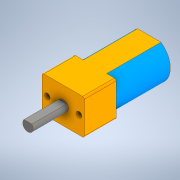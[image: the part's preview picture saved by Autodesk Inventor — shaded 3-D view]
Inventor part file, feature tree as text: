
AUTODESK INVENTOR PART (.ipt)
format: ipt  version: 2020 (Build 240168000, 168)  size: 167,424 bytes
history: native  units: mm
features: extrude x6, sketch x4, projected_geometry x2, fillet x1
ambient origin geometry x8: Origin, YZ Plane, XZ Plane, XY Plane, X Axis, Y Axis, Z Axis, Center Point
bodies: Solid1 (feature_tree)
feature tree (13):
  sketch  "Sketch1"  dims[d0=10.0mm d1=12.0mm]
  extrude  "Extrusion1"  Depth=12.0mm
  extrude  "Extrusion2"  Depth=9.0mm
  extrude  "Extrusion3"  Depth=9.0mm TaperAngle=0.0deg
  extrude  "Extrusion4"  Depth=10.0mm TaperAngle=0.0deg
  extrude  "Extrusion5"  Depth=0.5mm
  extrude  "Extrusion6"  Depth=9.8mm TaperAngle=0.0deg
  fillet  "Fillet1"  Radius=15.4mm
  sketch  "Sketch2"  dims[d2=9.0mm d3=1.6mm]
  projected_geometry  "Projected Loop1"
  sketch  "Sketch3"  dims[d4=3.0mm d5=9.0mm d6=0.0mm]
  projected_geometry  "Projected Loop2"
  sketch  "Sketch4"  dims[d7=0.0mm d8=0.0mm d9=10.0mm d10=0.0mm d11=1.0mm d12=9.8mm d13=0.0mm d14=15.4mm d15=0.0mm d16=5.0mm d17=0.8mm d18=0.0mm d19=0.5mm]
